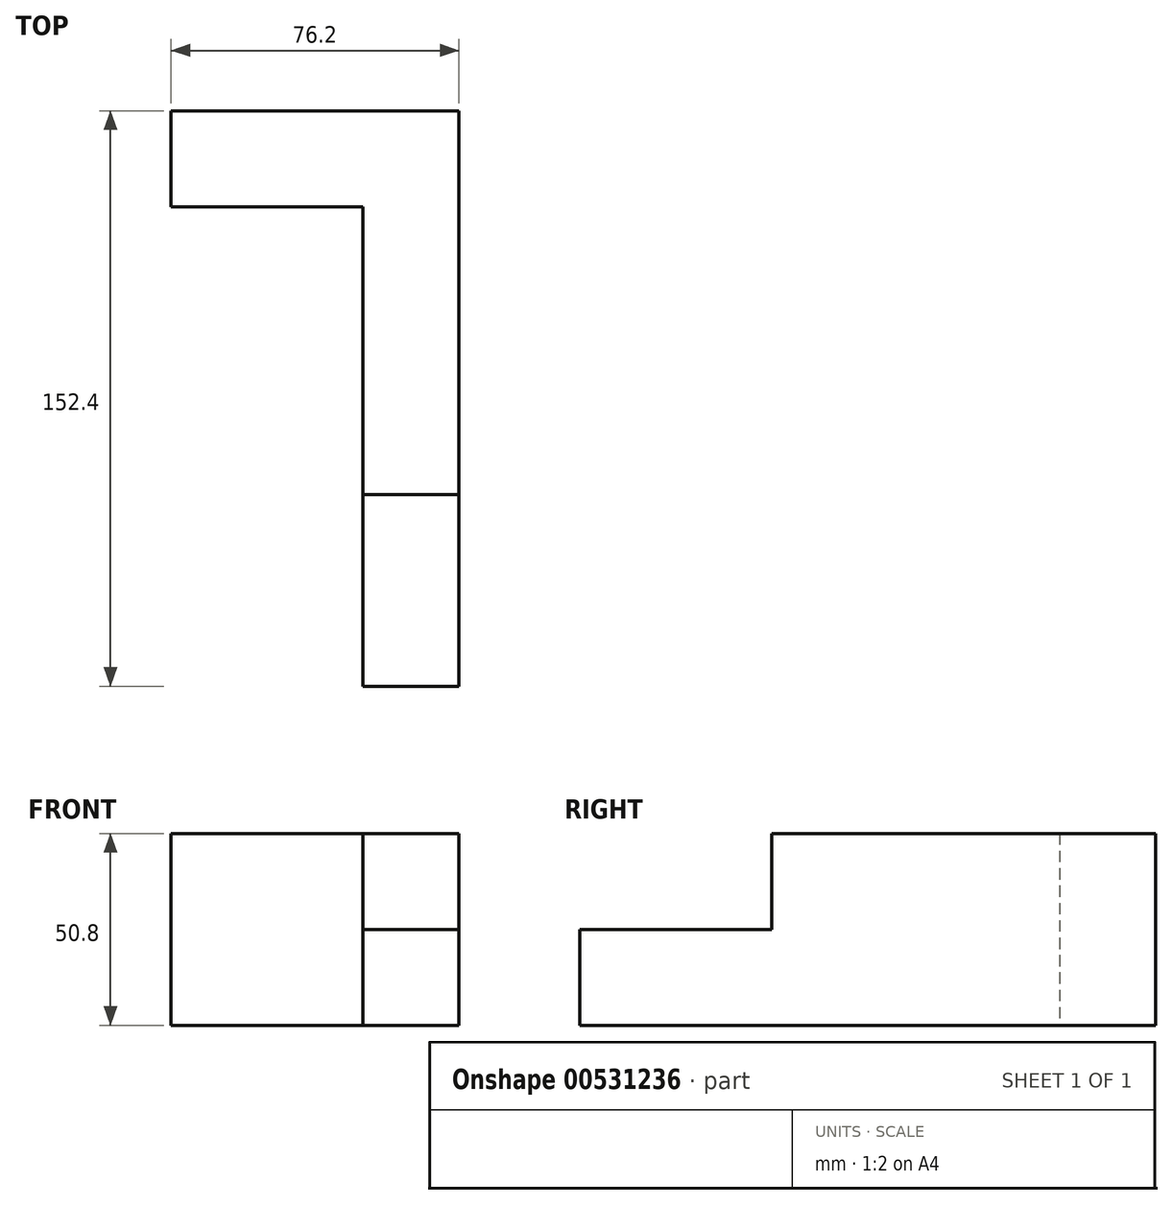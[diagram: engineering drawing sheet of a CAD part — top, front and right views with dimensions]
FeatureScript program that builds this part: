
annotation { "Feature Type Name" : "Feature", "Feature Type Description" : "" }
export const myFeature = defineFeature(function(context is Context, id is Id, definition is map)
    precondition{}
    {
        {
            var Q0;
            Q0=qCreatedBy(makeId("Top.planeOp"),FACE);
            var sketch = newSketch(context, id + "F0", { "sketchPlane" : qUnion([Q0])});
            skLineSegment(sketch, "E0", {"start": v(-80.36, 69.36) * mm, "end": v(-4.16, 69.36) * mm});
            skLineSegment(sketch, "E1", {"start": v(-4.16, 69.36) * mm, "end": v(-4.16, -83.04) * mm});
            skLineSegment(sketch, "E2", {"start": v(-80.36, 69.36) * mm, "end": v(-80.36, 43.96) * mm});
            skLineSegment(sketch, "E3", {"start": v(-80.36, 43.96) * mm, "end": v(-29.56, 43.96) * mm});
            skLineSegment(sketch, "E4", {"start": v(-29.56, 43.96) * mm, "end": v(-29.56, -83.04) * mm});
            skLineSegment(sketch, "E5", {"start": v(-29.56, -83.04) * mm, "end": v(-4.16, -83.04) * mm});
            skLineSegment(sketch, "E6.bottom", {"start": v(-29.56, -32.24) * mm, "end": v(-4.16, -32.24) * mm});
            skLineSegment(sketch, "E6.left", {"start": v(-29.56, -32.24) * mm, "end": v(-29.56, -83.04) * mm});
            skLineSegment(sketch, "E6.right", {"start": v(-4.16, -32.24) * mm, "end": v(-4.16, -83.04) * mm});
            skSolve(sketch);
        }
        {
            var Q0;
            Q0=makeQuery(id+"F0.imprint","IMPRINT",FACE,{"disambiguationData":[TD([[makeQuery(id+"F0.imprint","IMPRINT",EDGE,{"derivedFrom":sQuery(id+"F0.wireOp",EDGE,"E6.bottom")}),-1.0]])]});
            extrude(context, id + "F1", {"entities" : qUnion([Q0]), "depth" : 25.4 * mm, "offsetDistance" : 25.4 * mm});
        }
        {
            var Q0;
            Q0=makeQuery(id+"F0.imprint","IMPRINT",FACE,{"disambiguationData":[TD([[makeQuery(id+"F0.imprint","IMPRINT",EDGE,{"derivedFrom":sQuery(id+"F0.wireOp",EDGE,"E0")}),-1.0]])]});
            extrude(context, id + "F2", {"entities" : qUnion([Q0]), "operationType" : NewBodyOperationType.ADD, "depth" : 50.8 * mm, "offsetDistance" : 25.4 * mm});
        }
    });
